# Revit family: QF_BOURGEAT_Cuviers_Standards
name_source: partatom
category: Equipement spécialisé
revit_build: Autodesk Revit 2015 (Build: 20140606_1530(x64)
units: mm (PartAtom-declared; Revit-internal decimal feet)

## types (4) — shared parameters
Certification = NF Hygiene alimentaire
Fabricant = BOURGEAT
Hauteur hors tout = 1010 mm  [stored 3.31365 ft]
Spécification du Fabricant = Cuviers Standards
URL catalogue = http://www.bourgeat.fr

## per-type parameters (varying)
| type | BAc GN2/1+evac | Bac GN1/1 | Bac GN2/1 | CV en N | CV en U | Charge max | Cv en I | Largeur cadre | Longueur cadre | Longueur hors tout | Modèle | Poids net à vide | Profondeur hors tout | Remarques evacuation |
| Pour 1 GN2/1 ou 2GN1/1 | Non | Non | Oui | Non | Non | 60.00 kg | Oui | 535 mm  [stored 1.75525 ft] | 695 mm  [stored 2.28018 ft] | 770 mm  [stored 2.52625 ft] | 793506 | 10.00 kg | 630 mm  [stored 2.06693 ft] |  |
| Pour 1 GN2/1+ 1 GN1/1 ou 3 GN1/1 | Non | Oui | Non | Non | Non | 90.00 kg | Oui | 535 mm  [stored 1.75525 ft] | 1025 mm  [stored 3.36286 ft] | 1100 mm | 793706 | 10.50 kg | 630 mm  [stored 2.06693 ft] |  |
| Cuvier égouttoir pour 1 GN2/1 ou 2 GN1/1 | Oui | Non | Non | Non | Oui | 100.00 kg | Non | 545 mm  [stored 1.78806 ft] | 695 mm  [stored 2.28018 ft] | 770 mm  [stored 2.52625 ft] | 793906 | 16.00 kg | 640 mm  [stored 2.09974 ft] | 15/21 |
| Cuvier encastrable pour 1 GN2/1 | Non | Non | Non | Oui | Non | 60.00 kg | Non | 535 mm  [stored 1.75525 ft] | 695 mm  [stored 2.28018 ft] | 770 mm  [stored 2.52625 ft] | 793806 | 11.50 kg | 630 mm  [stored 2.06693 ft] |  |

note: [stored X ft] marks values corroborated as IEEE doubles in the binary element streams (Revit-internal decimal feet)
